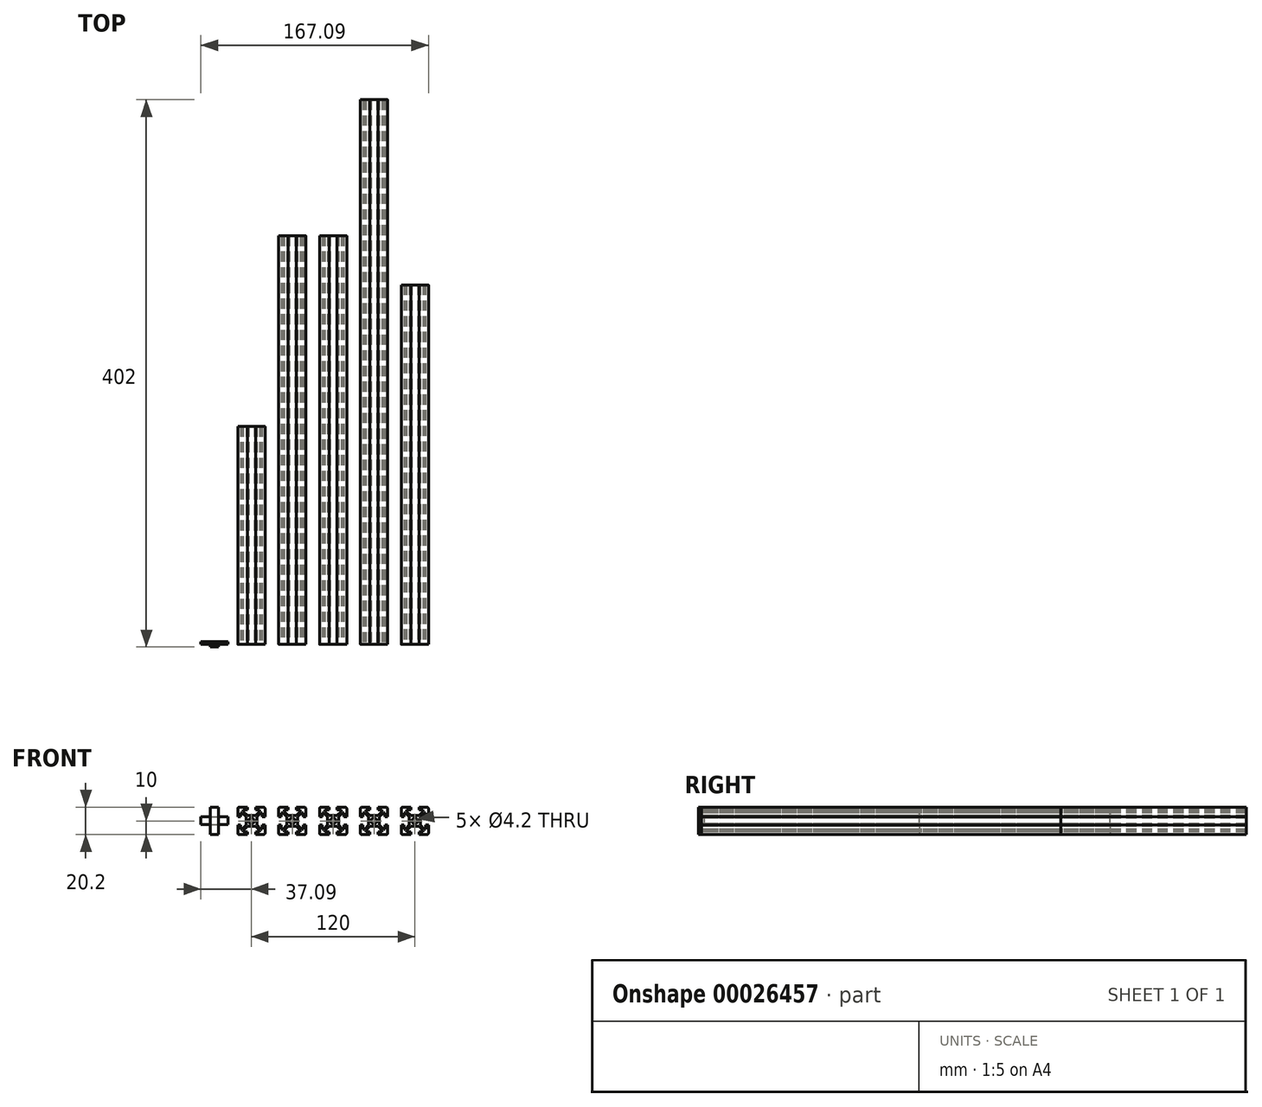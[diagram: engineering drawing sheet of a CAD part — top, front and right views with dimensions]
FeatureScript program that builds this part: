
annotation { "Feature Type Name" : "Feature", "Feature Type Description" : "" }
export const myFeature = defineFeature(function(context is Context, id is Id, definition is map)
    precondition{}
    {
        {
            var Q0;
            Q0=qCreatedBy(makeId("Front.planeOp"),FACE);
            var sketch = newSketch(context, id + "F0", { "sketchPlane" : qUnion([Q0])});
            skLineSegment(sketch, "E0", {"start": v(0, 4) * mm, "end": v(3, 4) * mm});
            skLineSegment(sketch, "E1", {"start": v(3, 4) * mm, "end": v(6, 7) * mm});
            skLineSegment(sketch, "E2", {"start": v(6, 7) * mm, "end": v(6, 8) * mm});
            skLineSegment(sketch, "E3", {"start": v(6, 8) * mm, "end": v(3, 8) * mm});
            skLineSegment(sketch, "E4", {"start": v(3, 8) * mm, "end": v(3, 10) * mm});
            skLineSegment(sketch, "E5", {"start": v(3, 10) * mm, "end": v(9, 10) * mm});
            skLineSegment(sketch, "E6", {"start": v(0, 0) * mm, "end": v(12.93, 12.93) * mm, "construction": true});
            skLineSegment(sketch, "E7.MirrorCS", {"start": v(4, 0) * mm, "end": v(4, 3) * mm});
            skLineSegment(sketch, "E8.MirrorCS", {"start": v(10, 3) * mm, "end": v(10, 9) * mm});
            skLineSegment(sketch, "E9.MirrorCS", {"start": v(8, 3) * mm, "end": v(10, 3) * mm});
            skLineSegment(sketch, "E10.MirrorCS", {"start": v(8, 6) * mm, "end": v(8, 3) * mm});
            skLineSegment(sketch, "E11.MirrorCS", {"start": v(4, 3) * mm, "end": v(7, 6) * mm});
            skLineSegment(sketch, "E12.MirrorCS", {"start": v(7, 6) * mm, "end": v(8, 6) * mm});
            skLineSegment(sketch, "E13.MirrorCS", {"start": v(-8, 3) * mm, "end": v(-10, 3) * mm});
            skLineSegment(sketch, "E14.MirrorCS", {"start": v(0, 4) * mm, "end": v(-3, 4) * mm});
            skLineSegment(sketch, "E15.MirrorCS", {"start": v(-3, 4) * mm, "end": v(-6, 7) * mm});
            skLineSegment(sketch, "E16.MirrorCS", {"start": v(-6, 7) * mm, "end": v(-6, 8) * mm});
            skLineSegment(sketch, "E17.MirrorCS", {"start": v(-6, 8) * mm, "end": v(-3, 8) * mm});
            skLineSegment(sketch, "E18.MirrorCS", {"start": v(-3, 8) * mm, "end": v(-3, 10) * mm});
            skLineSegment(sketch, "E19.MirrorCS", {"start": v(-3, 10) * mm, "end": v(-9, 10) * mm});
            skLineSegment(sketch, "E20.MirrorCS", {"start": v(-4, 0) * mm, "end": v(-4, 3) * mm});
            skLineSegment(sketch, "E21.MirrorCS", {"start": v(-10, 3) * mm, "end": v(-10, 9) * mm});
            skLineSegment(sketch, "E22.MirrorCS", {"start": v(-8, 6) * mm, "end": v(-8, 3) * mm});
            skLineSegment(sketch, "E23.MirrorCS", {"start": v(-4, 3) * mm, "end": v(-7, 6) * mm});
            skLineSegment(sketch, "E24.MirrorCS", {"start": v(-7, 6) * mm, "end": v(-8, 6) * mm});
            skLineSegment(sketch, "E25.MirrorCS", {"start": v(-7, -6) * mm, "end": v(-8, -6) * mm});
            skLineSegment(sketch, "E26.MirrorCS", {"start": v(-6, -7) * mm, "end": v(-6, -8) * mm});
            skLineSegment(sketch, "E27.MirrorCS", {"start": v(6, -7) * mm, "end": v(6, -8) * mm});
            skLineSegment(sketch, "E28.MirrorCS", {"start": v(7, -6) * mm, "end": v(8, -6) * mm});
            skLineSegment(sketch, "E29.MirrorCS", {"start": v(8, -3) * mm, "end": v(10, -3) * mm});
            skLineSegment(sketch, "E30.MirrorCS", {"start": v(-8, -3) * mm, "end": v(-10, -3) * mm});
            skLineSegment(sketch, "E31.MirrorCS", {"start": v(-6, -8) * mm, "end": v(-3, -8) * mm});
            skLineSegment(sketch, "E32.MirrorCS", {"start": v(-3, -10) * mm, "end": v(-9, -10) * mm});
            skLineSegment(sketch, "E33.MirrorCS", {"start": v(-4, -3) * mm, "end": v(-7, -6) * mm});
            skLineSegment(sketch, "E34.MirrorCS", {"start": v(-4, 0) * mm, "end": v(-4, -3) * mm});
            skLineSegment(sketch, "E35.MirrorCS", {"start": v(-3, -8) * mm, "end": v(-3, -10) * mm});
            skLineSegment(sketch, "E36.MirrorCS", {"start": v(0, -4) * mm, "end": v(-3, -4) * mm});
            skLineSegment(sketch, "E37.MirrorCS", {"start": v(0, -4) * mm, "end": v(3, -4) * mm});
            skLineSegment(sketch, "E38.MirrorCS", {"start": v(6, -8) * mm, "end": v(3, -8) * mm});
            skLineSegment(sketch, "E39.MirrorCS", {"start": v(3, -8) * mm, "end": v(3, -10) * mm});
            skLineSegment(sketch, "E40.MirrorCS", {"start": v(3, -10) * mm, "end": v(9, -10) * mm});
            skLineSegment(sketch, "E41.MirrorCS", {"start": v(3, -4) * mm, "end": v(6, -7) * mm});
            skLineSegment(sketch, "E42.MirrorCS", {"start": v(-3, -4) * mm, "end": v(-6, -7) * mm});
            skLineSegment(sketch, "E43.MirrorCS", {"start": v(4, 0) * mm, "end": v(4, -3) * mm});
            skLineSegment(sketch, "E44.MirrorCS", {"start": v(10, -3) * mm, "end": v(10, -9) * mm});
            skLineSegment(sketch, "E45.MirrorCS", {"start": v(8, -6) * mm, "end": v(8, -3) * mm});
            skLineSegment(sketch, "E46.MirrorCS", {"start": v(4, -3) * mm, "end": v(7, -6) * mm});
            skLineSegment(sketch, "E47.MirrorCS", {"start": v(-8, -6) * mm, "end": v(-8, -3) * mm});
            skLineSegment(sketch, "E48.MirrorCS", {"start": v(-10, -3) * mm, "end": v(-10, -9) * mm});
            skCircle(sketch, "E49", {"center": v(0, 0) * mm, "radius": 2.1 * mm});
            skPoint(sketch, "E50.visualSharp", {"position": v(-10, 10) * mm});
            skArc(sketch, "E50.filletArc", {"start": v(-9, 10) * mm, "mid": v(-9.7, 9.7) * mm, "end": v(-10, 9) * mm});
            skPoint(sketch, "E51.visualSharp", {"position": v(10, 10) * mm});
            skArc(sketch, "E51.filletArc", {"start": v(10, 9) * mm, "mid": v(9.7, 9.7) * mm, "end": v(9, 10) * mm});
            skPoint(sketch, "E52.visualSharp", {"position": v(10, -10) * mm});
            skArc(sketch, "E52.filletArc", {"start": v(9, -10) * mm, "mid": v(9.7, -9.7) * mm, "end": v(10, -9) * mm});
            skPoint(sketch, "E53.visualSharp", {"position": v(-10, -10) * mm});
            skArc(sketch, "E53.filletArc", {"start": v(-10, -9) * mm, "mid": v(-9.7, -9.7) * mm, "end": v(-9, -10) * mm});
            skLineSegment(sketch, "E54", {"start": v(-3, 4) * mm, "end": v(-3, 8) * mm, "construction": true});
            skLineSegment(sketch, "E55", {"start": v(3, 4) * mm, "end": v(3, 8) * mm, "construction": true});
            skSolve(sketch);
        }
        {
            var Q0;
            Q0=makeQuery(id+"F0.imprint","IMPRINT",FACE,{"disambiguationData":[TD([[makeQuery(id+"F0.imprint","IMPRINT",EDGE,{"derivedFrom":sQuery(id+"F0.wireOp",EDGE,"E0")}),-1.0]])]});
            extrude(context, id + "F1", {"entities" : qUnion([Q0]), "oppositeDirection" : true, "depth" : 160 * mm});
        }
        {
            var Q0;
            Q0 = qSketchRegion(id + "F0", true);
            extrude(context, id + "F2", {"entities" : qUnion([Q0]), "oppositeDirection" : true, "depth" : 300 * mm});
        }
        {
            var Q0;
            Q0 = qSketchRegion(id + "F0", true);
            extrude(context, id + "F3", {"entities" : qUnion([Q0]), "oppositeDirection" : true, "depth" : 400 * mm});
        }
        {
            var Q0;
            Q0=makeQuery(id+"F2.opExtrude","SWEPT_BODY",BODY,{"disambiguationData":[OSD([sQuery(id+"F0.wireOp",EDGE,"E0"),sQuery(id+"F0.wireOp",EDGE,"E1"),sQuery(id+"F0.wireOp",EDGE,"E2"),sQuery(id+"F0.wireOp",EDGE,"E3"),sQuery(id+"F0.wireOp",EDGE,"E4"),sQuery(id+"F0.wireOp",EDGE,"E5"),sQuery(id+"F0.wireOp",EDGE,"E7.MirrorCS"),sQuery(id+"F0.wireOp",EDGE,"E8.MirrorCS"),sQuery(id+"F0.wireOp",EDGE,"E10.MirrorCS"),sQuery(id+"F0.wireOp",EDGE,"E11.MirrorCS"),sQuery(id+"F0.wireOp",EDGE,"E12.MirrorCS"),sQuery(id+"F0.wireOp",EDGE,"E9.MirrorCS"),sQuery(id+"F0.wireOp",EDGE,"E14.MirrorCS"),sQuery(id+"F0.wireOp",EDGE,"E15.MirrorCS"),sQuery(id+"F0.wireOp",EDGE,"E16.MirrorCS"),sQuery(id+"F0.wireOp",EDGE,"E17.MirrorCS"),sQuery(id+"F0.wireOp",EDGE,"E18.MirrorCS"),sQuery(id+"F0.wireOp",EDGE,"E19.MirrorCS"),sQuery(id+"F0.wireOp",EDGE,"E20.MirrorCS"),sQuery(id+"F0.wireOp",EDGE,"E21.MirrorCS"),sQuery(id+"F0.wireOp",EDGE,"E22.MirrorCS"),sQuery(id+"F0.wireOp",EDGE,"E23.MirrorCS"),sQuery(id+"F0.wireOp",EDGE,"E13.MirrorCS"),sQuery(id+"F0.wireOp",EDGE,"E24.MirrorCS"),sQuery(id+"F0.wireOp",EDGE,"E25.MirrorCS"),sQuery(id+"F0.wireOp",EDGE,"E26.MirrorCS"),sQuery(id+"F0.wireOp",EDGE,"E27.MirrorCS"),sQuery(id+"F0.wireOp",EDGE,"E28.MirrorCS"),sQuery(id+"F0.wireOp",EDGE,"E31.MirrorCS"),sQuery(id+"F0.wireOp",EDGE,"E32.MirrorCS"),sQuery(id+"F0.wireOp",EDGE,"E33.MirrorCS"),sQuery(id+"F0.wireOp",EDGE,"E34.MirrorCS"),sQuery(id+"F0.wireOp",EDGE,"E35.MirrorCS"),sQuery(id+"F0.wireOp",EDGE,"E36.MirrorCS"),sQuery(id+"F0.wireOp",EDGE,"E37.MirrorCS"),sQuery(id+"F0.wireOp",EDGE,"E38.MirrorCS"),sQuery(id+"F0.wireOp",EDGE,"E39.MirrorCS"),sQuery(id+"F0.wireOp",EDGE,"E40.MirrorCS"),sQuery(id+"F0.wireOp",EDGE,"E41.MirrorCS"),sQuery(id+"F0.wireOp",EDGE,"E42.MirrorCS"),sQuery(id+"F0.wireOp",EDGE,"E43.MirrorCS"),sQuery(id+"F0.wireOp",EDGE,"E44.MirrorCS"),sQuery(id+"F0.wireOp",EDGE,"E29.MirrorCS"),sQuery(id+"F0.wireOp",EDGE,"E45.MirrorCS"),sQuery(id+"F0.wireOp",EDGE,"E46.MirrorCS"),sQuery(id+"F0.wireOp",EDGE,"E47.MirrorCS"),sQuery(id+"F0.wireOp",EDGE,"E48.MirrorCS"),sQuery(id+"F0.wireOp",EDGE,"E30.MirrorCS"),sQuery(id+"F0.wireOp",EDGE,"E49"),sQuery(id+"F0.wireOp",EDGE,"E50.filletArc"),sQuery(id+"F0.wireOp",EDGE,"E51.filletArc"),sQuery(id+"F0.wireOp",EDGE,"E52.filletArc"),sQuery(id+"F0.wireOp",EDGE,"E53.filletArc")])]});
            transform(context, id + "F4", {"entities" : qUnion([Q0]), "transformType" : TransformType.TRANSLATION_3D, "dx" : 60 * mm, "dy" : 0 * mm, "dz" : 0 * mm, "makeCopy" : false});
        }
        {
            var Q0;
            Q0=makeQuery(id+"F3.opExtrude","SWEPT_BODY",BODY,{"disambiguationData":[OSD([sQuery(id+"F0.wireOp",EDGE,"E0"),sQuery(id+"F0.wireOp",EDGE,"E1"),sQuery(id+"F0.wireOp",EDGE,"E2"),sQuery(id+"F0.wireOp",EDGE,"E3"),sQuery(id+"F0.wireOp",EDGE,"E4"),sQuery(id+"F0.wireOp",EDGE,"E5"),sQuery(id+"F0.wireOp",EDGE,"E7.MirrorCS"),sQuery(id+"F0.wireOp",EDGE,"E8.MirrorCS"),sQuery(id+"F0.wireOp",EDGE,"E10.MirrorCS"),sQuery(id+"F0.wireOp",EDGE,"E11.MirrorCS"),sQuery(id+"F0.wireOp",EDGE,"E12.MirrorCS"),sQuery(id+"F0.wireOp",EDGE,"E9.MirrorCS"),sQuery(id+"F0.wireOp",EDGE,"E14.MirrorCS"),sQuery(id+"F0.wireOp",EDGE,"E15.MirrorCS"),sQuery(id+"F0.wireOp",EDGE,"E16.MirrorCS"),sQuery(id+"F0.wireOp",EDGE,"E17.MirrorCS"),sQuery(id+"F0.wireOp",EDGE,"E18.MirrorCS"),sQuery(id+"F0.wireOp",EDGE,"E19.MirrorCS"),sQuery(id+"F0.wireOp",EDGE,"E20.MirrorCS"),sQuery(id+"F0.wireOp",EDGE,"E21.MirrorCS"),sQuery(id+"F0.wireOp",EDGE,"E22.MirrorCS"),sQuery(id+"F0.wireOp",EDGE,"E23.MirrorCS"),sQuery(id+"F0.wireOp",EDGE,"E13.MirrorCS"),sQuery(id+"F0.wireOp",EDGE,"E24.MirrorCS"),sQuery(id+"F0.wireOp",EDGE,"E25.MirrorCS"),sQuery(id+"F0.wireOp",EDGE,"E26.MirrorCS"),sQuery(id+"F0.wireOp",EDGE,"E27.MirrorCS"),sQuery(id+"F0.wireOp",EDGE,"E28.MirrorCS"),sQuery(id+"F0.wireOp",EDGE,"E31.MirrorCS"),sQuery(id+"F0.wireOp",EDGE,"E32.MirrorCS"),sQuery(id+"F0.wireOp",EDGE,"E33.MirrorCS"),sQuery(id+"F0.wireOp",EDGE,"E34.MirrorCS"),sQuery(id+"F0.wireOp",EDGE,"E35.MirrorCS"),sQuery(id+"F0.wireOp",EDGE,"E36.MirrorCS"),sQuery(id+"F0.wireOp",EDGE,"E37.MirrorCS"),sQuery(id+"F0.wireOp",EDGE,"E38.MirrorCS"),sQuery(id+"F0.wireOp",EDGE,"E39.MirrorCS"),sQuery(id+"F0.wireOp",EDGE,"E40.MirrorCS"),sQuery(id+"F0.wireOp",EDGE,"E41.MirrorCS"),sQuery(id+"F0.wireOp",EDGE,"E42.MirrorCS"),sQuery(id+"F0.wireOp",EDGE,"E43.MirrorCS"),sQuery(id+"F0.wireOp",EDGE,"E44.MirrorCS"),sQuery(id+"F0.wireOp",EDGE,"E29.MirrorCS"),sQuery(id+"F0.wireOp",EDGE,"E45.MirrorCS"),sQuery(id+"F0.wireOp",EDGE,"E46.MirrorCS"),sQuery(id+"F0.wireOp",EDGE,"E47.MirrorCS"),sQuery(id+"F0.wireOp",EDGE,"E48.MirrorCS"),sQuery(id+"F0.wireOp",EDGE,"E30.MirrorCS"),sQuery(id+"F0.wireOp",EDGE,"E49"),sQuery(id+"F0.wireOp",EDGE,"E50.filletArc"),sQuery(id+"F0.wireOp",EDGE,"E51.filletArc"),sQuery(id+"F0.wireOp",EDGE,"E52.filletArc"),sQuery(id+"F0.wireOp",EDGE,"E53.filletArc")])]});
            transform(context, id + "F5", {"entities" : qUnion([Q0]), "transformType" : TransformType.TRANSLATION_3D, "dx" : 90 * mm, "dy" : 0 * mm, "dz" : 0 * mm, "makeCopy" : false});
        }
        {
            var Q0;
            Q0=qCreatedBy(makeId("Front.planeOp"),FACE);
            var sketch = newSketch(context, id + "F6", { "sketchPlane" : qUnion([Q0])});
            skLineSegment(sketch, "E56.bottom", {"start": v(-37.1, 10.2) * mm, "end": v(-17.1, 10.2) * mm});
            skLineSegment(sketch, "E56.top", {"start": v(-37.1, -9.8) * mm, "end": v(-17.1, -9.8) * mm});
            skLineSegment(sketch, "E56.left", {"start": v(-37.1, 10.2) * mm, "end": v(-37.1, -9.8) * mm});
            skLineSegment(sketch, "E56.right", {"start": v(-17.1, 10.2) * mm, "end": v(-17.1, -9.8) * mm});
            skLineSegment(sketch, "E57", {"start": v(-30.1, 10.2) * mm, "end": v(-30.1, -9.8) * mm});
            skLineSegment(sketch, "E58", {"start": v(-24.1, 10.2) * mm, "end": v(-24.1, -9.8) * mm});
            skLineSegment(sketch, "E59", {"start": v(-37.1, -2.8) * mm, "end": v(-17.1, -2.8) * mm});
            skLineSegment(sketch, "E60", {"start": v(-37.1, 3.2) * mm, "end": v(-17.1, 3.2) * mm});
            skLineSegment(sketch, "E61", {"start": v(-30.1, 3.2) * mm, "end": v(-24.1, -2.8) * mm, "construction": true});
            skLineSegment(sketch, "E62", {"start": v(-24.1, 3.2) * mm, "end": v(-30.1, -2.8) * mm, "construction": true});
            skPoint(sketch, "E63", {"position": v(-27.1, 0.2) * mm});
            skSolve(sketch);
        }
        {
            var Q0;
            {var subQ3=sQuery(id+"F6.wireOp",EDGE,"E57");var subQ5=sQuery(id+"F6.wireOp",EDGE,"E56.bottom");var subQ7=makeQuery(id+"F6.imprint","INTERSECT",VERTEX,{"derivedFrom":[subQ5,subQ3]});Q0=makeQuery(id+"F6.imprint","IMPRINT",FACE,{"disambiguationData":[TD([[makeQuery(id+"F6.imprint","IMPRINT",EDGE,{"disambiguationData":[TD([[subQ7,-1.0]])],"derivedFrom":subQ5}),-1.0]])]});}
            var Q1;
            {var subQ0=sQuery(id+"F6.wireOp",EDGE,"E60");var subQ3=sQuery(id+"F6.wireOp",EDGE,"E57");var subQ4=makeQuery(id+"F6.imprint","INTERSECT",VERTEX,{"derivedFrom":[subQ3,subQ0]});Q1=makeQuery(id+"F6.imprint","IMPRINT",FACE,{"disambiguationData":[TD([[makeQuery(id+"F6.imprint","IMPRINT",EDGE,{"disambiguationData":[TD([[subQ4,-1.0]])],"derivedFrom":subQ3}),1.0]])]});}
            var Q2;
            {var subQ3=sQuery(id+"F6.wireOp",EDGE,"E57");var subQ5=sQuery(id+"F6.wireOp",EDGE,"E56.top");var subQ7=makeQuery(id+"F6.imprint","INTERSECT",VERTEX,{"derivedFrom":[subQ5,subQ3]});Q2=makeQuery(id+"F6.imprint","IMPRINT",FACE,{"disambiguationData":[TD([[makeQuery(id+"F6.imprint","IMPRINT",EDGE,{"disambiguationData":[TD([[subQ7,-1.0]])],"derivedFrom":subQ5}),1.0]])]});}
            extrude(context, id + "F7", {"entities" : qUnion([Q0, Q1, Q2]), "depth" : 2 * mm});
        }
        {
            var Q0;
            {var subQ3=sQuery(id+"F6.wireOp",EDGE,"E56.left");var subQ5=sQuery(id+"F6.wireOp",EDGE,"E59");var subQ7=makeQuery(id+"F6.imprint","INTERSECT",VERTEX,{"derivedFrom":[subQ3,subQ5]});Q0=makeQuery(id+"F6.imprint","IMPRINT",FACE,{"disambiguationData":[TD([[makeQuery(id+"F6.imprint","IMPRINT",EDGE,{"disambiguationData":[TD([[subQ7,1.0]])],"derivedFrom":subQ3}),1.0]])]});}
            var Q1;
            {var subQ0=sQuery(id+"F6.wireOp",EDGE,"E60");var subQ3=sQuery(id+"F6.wireOp",EDGE,"E57");var subQ4=makeQuery(id+"F6.imprint","INTERSECT",VERTEX,{"derivedFrom":[subQ3,subQ0]});Q1=makeQuery(id+"F6.imprint","IMPRINT",FACE,{"disambiguationData":[TD([[makeQuery(id+"F6.imprint","IMPRINT",EDGE,{"disambiguationData":[TD([[subQ4,-1.0]])],"derivedFrom":subQ3}),1.0]])]});}
            var Q2;
            {var subQ3=sQuery(id+"F6.wireOp",EDGE,"E56.right");var subQ5=sQuery(id+"F6.wireOp",EDGE,"E59");var subQ7=makeQuery(id+"F6.imprint","INTERSECT",VERTEX,{"derivedFrom":[subQ3,subQ5]});Q2=makeQuery(id+"F6.imprint","IMPRINT",FACE,{"disambiguationData":[TD([[makeQuery(id+"F6.imprint","IMPRINT",EDGE,{"disambiguationData":[TD([[subQ7,1.0]])],"derivedFrom":subQ3}),-1.0]])]});}
            extrude(context, id + "F8", {"entities" : qUnion([Q0, Q1, Q2]), "operationType" : NewBodyOperationType.ADD, "oppositeDirection" : true, "depth" : 2 * mm});
        }
        {
            var Q0;
            Q0=makeQuery(id+"F2.opExtrude","SWEPT_FACE",FACE,{"disambiguationData":[OSD([sQuery(id+"F0.wireOp",EDGE,"E5")])]});
            var sketch = newSketch(context, id + "F9", { "sketchPlane" : qUnion([Q0])});
            skLineSegment(sketch, "E64.0", {"start": v(50, 300) * mm, "end": v(50, 0) * mm, "construction": true});
            skLineSegment(sketch, "E65.1", {"start": v(70, 300) * mm, "end": v(70, 0) * mm, "construction": true});
            skLineSegment(sketch, "E66", {"start": v(50, 150) * mm, "end": v(70, 150) * mm, "construction": true});
            skPoint(sketch, "E67", {"position": v(60, 150) * mm});
            skPoint(sketch, "E68", {"position": v(33.74, 152.67) * mm});
            skLineSegment(sketch, "E69", {"start": v(60, 70) * mm, "end": v(60, 230) * mm, "construction": true});
            skPoint(sketch, "E70", {"position": v(60, 70) * mm});
            skPoint(sketch, "E71", {"position": v(60, 230) * mm});
            skPoint(sketch, "E72", {"position": v(27.74, 198.96) * mm});
            skSolve(sketch);
        }
        {
            var Q0;
            Q0=makeQuery(id+"F3.opExtrude","SWEPT_FACE",FACE,{"disambiguationData":[OSD([sQuery(id+"F0.wireOp",EDGE,"E19.MirrorCS")])]});
            var sketch = newSketch(context, id + "F10", { "sketchPlane" : qUnion([Q0])});
            skLineSegment(sketch, "E73", {"start": v(90, 0) * mm, "end": v(90, 10) * mm, "construction": true});
            skPoint(sketch, "E74", {"position": v(90, 390) * mm});
            skLineSegment(sketch, "E75", {"start": v(80, 200) * mm, "end": v(100, 200) * mm, "construction": true});
            skLineSegment(sketch, "E76.1", {"start": v(100, 400) * mm, "end": v(100, 0) * mm, "construction": true});
            skLineSegment(sketch, "E77.1", {"start": v(80, 400) * mm, "end": v(80, 0) * mm, "construction": true});
            skPoint(sketch, "E78", {"position": v(90, 200) * mm});
            skSolve(sketch);
        }
        {
            var Q0;
            Q0 = qSketchRegion(id + "F0", true);
            extrude(context, id + "F11", {"entities" : qUnion([Q0]), "oppositeDirection" : true, "depth" : 300 * mm});
        }
        {
            var Q0;
            Q0=makeQuery(id+"F11.opExtrude","SWEPT_BODY",BODY,{"disambiguationData":[OSD([sQuery(id+"F0.wireOp",EDGE,"E0"),sQuery(id+"F0.wireOp",EDGE,"E1"),sQuery(id+"F0.wireOp",EDGE,"E2"),sQuery(id+"F0.wireOp",EDGE,"E3"),sQuery(id+"F0.wireOp",EDGE,"E4"),sQuery(id+"F0.wireOp",EDGE,"E5"),sQuery(id+"F0.wireOp",EDGE,"E7.MirrorCS"),sQuery(id+"F0.wireOp",EDGE,"E8.MirrorCS"),sQuery(id+"F0.wireOp",EDGE,"E10.MirrorCS"),sQuery(id+"F0.wireOp",EDGE,"E11.MirrorCS"),sQuery(id+"F0.wireOp",EDGE,"E12.MirrorCS"),sQuery(id+"F0.wireOp",EDGE,"E9.MirrorCS"),sQuery(id+"F0.wireOp",EDGE,"E14.MirrorCS"),sQuery(id+"F0.wireOp",EDGE,"E15.MirrorCS"),sQuery(id+"F0.wireOp",EDGE,"E16.MirrorCS"),sQuery(id+"F0.wireOp",EDGE,"E17.MirrorCS"),sQuery(id+"F0.wireOp",EDGE,"E18.MirrorCS"),sQuery(id+"F0.wireOp",EDGE,"E19.MirrorCS"),sQuery(id+"F0.wireOp",EDGE,"E20.MirrorCS"),sQuery(id+"F0.wireOp",EDGE,"E21.MirrorCS"),sQuery(id+"F0.wireOp",EDGE,"E22.MirrorCS"),sQuery(id+"F0.wireOp",EDGE,"E23.MirrorCS"),sQuery(id+"F0.wireOp",EDGE,"E13.MirrorCS"),sQuery(id+"F0.wireOp",EDGE,"E24.MirrorCS"),sQuery(id+"F0.wireOp",EDGE,"E25.MirrorCS"),sQuery(id+"F0.wireOp",EDGE,"E26.MirrorCS"),sQuery(id+"F0.wireOp",EDGE,"E27.MirrorCS"),sQuery(id+"F0.wireOp",EDGE,"E28.MirrorCS"),sQuery(id+"F0.wireOp",EDGE,"E31.MirrorCS"),sQuery(id+"F0.wireOp",EDGE,"E32.MirrorCS"),sQuery(id+"F0.wireOp",EDGE,"E33.MirrorCS"),sQuery(id+"F0.wireOp",EDGE,"E34.MirrorCS"),sQuery(id+"F0.wireOp",EDGE,"E35.MirrorCS"),sQuery(id+"F0.wireOp",EDGE,"E36.MirrorCS"),sQuery(id+"F0.wireOp",EDGE,"E37.MirrorCS"),sQuery(id+"F0.wireOp",EDGE,"E38.MirrorCS"),sQuery(id+"F0.wireOp",EDGE,"E39.MirrorCS"),sQuery(id+"F0.wireOp",EDGE,"E40.MirrorCS"),sQuery(id+"F0.wireOp",EDGE,"E41.MirrorCS"),sQuery(id+"F0.wireOp",EDGE,"E42.MirrorCS"),sQuery(id+"F0.wireOp",EDGE,"E43.MirrorCS"),sQuery(id+"F0.wireOp",EDGE,"E44.MirrorCS"),sQuery(id+"F0.wireOp",EDGE,"E29.MirrorCS"),sQuery(id+"F0.wireOp",EDGE,"E45.MirrorCS"),sQuery(id+"F0.wireOp",EDGE,"E46.MirrorCS"),sQuery(id+"F0.wireOp",EDGE,"E47.MirrorCS"),sQuery(id+"F0.wireOp",EDGE,"E48.MirrorCS"),sQuery(id+"F0.wireOp",EDGE,"E30.MirrorCS"),sQuery(id+"F0.wireOp",EDGE,"E49"),sQuery(id+"F0.wireOp",EDGE,"E50.filletArc"),sQuery(id+"F0.wireOp",EDGE,"E51.filletArc"),sQuery(id+"F0.wireOp",EDGE,"E52.filletArc"),sQuery(id+"F0.wireOp",EDGE,"E53.filletArc")])]});
            transform(context, id + "F12", {"entities" : qUnion([Q0]), "transformType" : TransformType.TRANSLATION_3D, "dx" : 30 * mm, "dy" : 0 * mm, "dz" : 0 * mm, "makeCopy" : false});
        }
        {
            var Q0;
            Q0 = qSketchRegion(id + "F0", true);
            extrude(context, id + "F13", {"entities" : qUnion([Q0]), "oppositeDirection" : true, "depth" : (300 - (18 * 2)) * mm});
        }
        {
            var Q0;
            Q0=makeQuery(id+"F13.opExtrude","SWEPT_BODY",BODY,{"disambiguationData":[OSD([sQuery(id+"F0.wireOp",EDGE,"E0"),sQuery(id+"F0.wireOp",EDGE,"E1"),sQuery(id+"F0.wireOp",EDGE,"E2"),sQuery(id+"F0.wireOp",EDGE,"E3"),sQuery(id+"F0.wireOp",EDGE,"E4"),sQuery(id+"F0.wireOp",EDGE,"E5"),sQuery(id+"F0.wireOp",EDGE,"E7.MirrorCS"),sQuery(id+"F0.wireOp",EDGE,"E8.MirrorCS"),sQuery(id+"F0.wireOp",EDGE,"E10.MirrorCS"),sQuery(id+"F0.wireOp",EDGE,"E11.MirrorCS"),sQuery(id+"F0.wireOp",EDGE,"E12.MirrorCS"),sQuery(id+"F0.wireOp",EDGE,"E9.MirrorCS"),sQuery(id+"F0.wireOp",EDGE,"E14.MirrorCS"),sQuery(id+"F0.wireOp",EDGE,"E15.MirrorCS"),sQuery(id+"F0.wireOp",EDGE,"E16.MirrorCS"),sQuery(id+"F0.wireOp",EDGE,"E17.MirrorCS"),sQuery(id+"F0.wireOp",EDGE,"E18.MirrorCS"),sQuery(id+"F0.wireOp",EDGE,"E19.MirrorCS"),sQuery(id+"F0.wireOp",EDGE,"E20.MirrorCS"),sQuery(id+"F0.wireOp",EDGE,"E21.MirrorCS"),sQuery(id+"F0.wireOp",EDGE,"E22.MirrorCS"),sQuery(id+"F0.wireOp",EDGE,"E23.MirrorCS"),sQuery(id+"F0.wireOp",EDGE,"E13.MirrorCS"),sQuery(id+"F0.wireOp",EDGE,"E24.MirrorCS"),sQuery(id+"F0.wireOp",EDGE,"E25.MirrorCS"),sQuery(id+"F0.wireOp",EDGE,"E26.MirrorCS"),sQuery(id+"F0.wireOp",EDGE,"E27.MirrorCS"),sQuery(id+"F0.wireOp",EDGE,"E28.MirrorCS"),sQuery(id+"F0.wireOp",EDGE,"E31.MirrorCS"),sQuery(id+"F0.wireOp",EDGE,"E32.MirrorCS"),sQuery(id+"F0.wireOp",EDGE,"E33.MirrorCS"),sQuery(id+"F0.wireOp",EDGE,"E34.MirrorCS"),sQuery(id+"F0.wireOp",EDGE,"E35.MirrorCS"),sQuery(id+"F0.wireOp",EDGE,"E36.MirrorCS"),sQuery(id+"F0.wireOp",EDGE,"E37.MirrorCS"),sQuery(id+"F0.wireOp",EDGE,"E38.MirrorCS"),sQuery(id+"F0.wireOp",EDGE,"E39.MirrorCS"),sQuery(id+"F0.wireOp",EDGE,"E40.MirrorCS"),sQuery(id+"F0.wireOp",EDGE,"E41.MirrorCS"),sQuery(id+"F0.wireOp",EDGE,"E42.MirrorCS"),sQuery(id+"F0.wireOp",EDGE,"E43.MirrorCS"),sQuery(id+"F0.wireOp",EDGE,"E44.MirrorCS"),sQuery(id+"F0.wireOp",EDGE,"E29.MirrorCS"),sQuery(id+"F0.wireOp",EDGE,"E45.MirrorCS"),sQuery(id+"F0.wireOp",EDGE,"E46.MirrorCS"),sQuery(id+"F0.wireOp",EDGE,"E47.MirrorCS"),sQuery(id+"F0.wireOp",EDGE,"E48.MirrorCS"),sQuery(id+"F0.wireOp",EDGE,"E30.MirrorCS"),sQuery(id+"F0.wireOp",EDGE,"E49"),sQuery(id+"F0.wireOp",EDGE,"E50.filletArc"),sQuery(id+"F0.wireOp",EDGE,"E51.filletArc"),sQuery(id+"F0.wireOp",EDGE,"E52.filletArc"),sQuery(id+"F0.wireOp",EDGE,"E53.filletArc")])]});
            transform(context, id + "F14", {"entities" : qUnion([Q0]), "transformType" : TransformType.TRANSLATION_3D, "dx" : 120 * mm, "dy" : 0 * mm, "dz" : 0 * mm, "makeCopy" : false});
        }
    });
